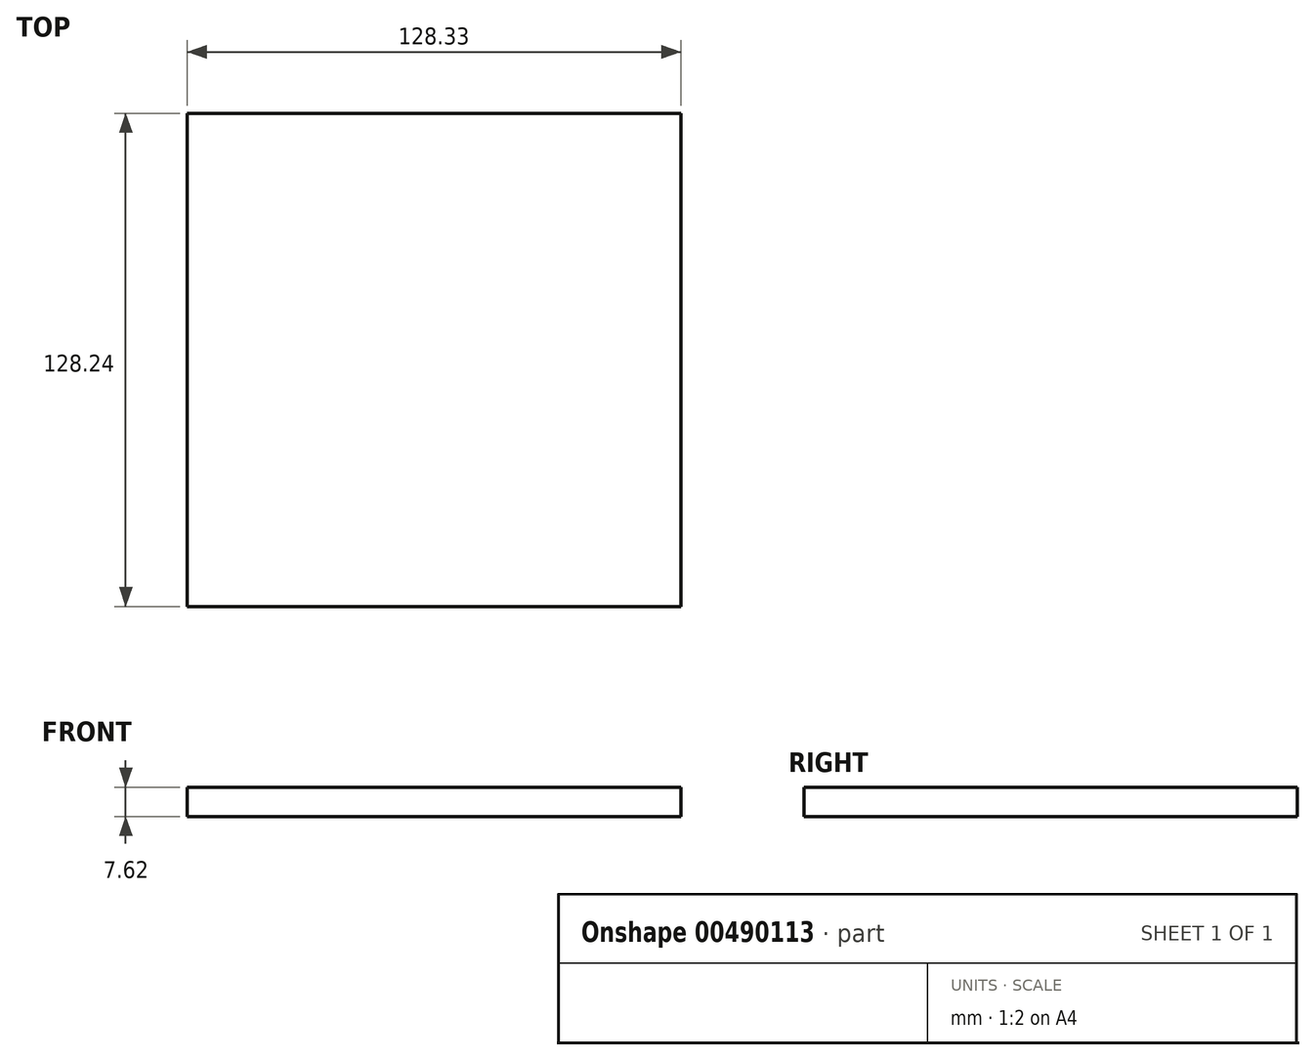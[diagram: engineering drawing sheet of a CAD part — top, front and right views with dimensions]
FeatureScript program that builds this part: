
annotation { "Feature Type Name" : "Feature", "Feature Type Description" : "" }
export const myFeature = defineFeature(function(context is Context, id is Id, definition is map)
    precondition{}
    {
        {
            var Q0;
            Q0=qCreatedBy(makeId("Top.planeOp"),FACE);
            var sketch = newSketch(context, id + "F0", { "sketchPlane" : qUnion([Q0])});
            skLineSegment(sketch, "E0.bottom", {"start": v(-62.73, 65.3) * mm, "end": v(65.6, 65.3) * mm});
            skLineSegment(sketch, "E0.top", {"start": v(-62.73, -62.94) * mm, "end": v(65.6, -62.94) * mm});
            skLineSegment(sketch, "E0.left", {"start": v(-62.73, 65.3) * mm, "end": v(-62.73, -62.94) * mm});
            skLineSegment(sketch, "E0.right", {"start": v(65.6, 65.3) * mm, "end": v(65.6, -62.94) * mm});
            skSolve(sketch);
        }
        {
            var Q0;
            Q0=makeQuery(id+"F0.imprint","IMPRINT",FACE,{"disambiguationData":[TD([[makeQuery(id+"F0.imprint","IMPRINT",EDGE,{"derivedFrom":sQuery(id+"F0.wireOp",EDGE,"E0.bottom")}),-1.0]])]});
            extrude(context, id + "F1", {"entities" : qUnion([Q0]), "depth" : 7.62 * mm});
        }
    });
